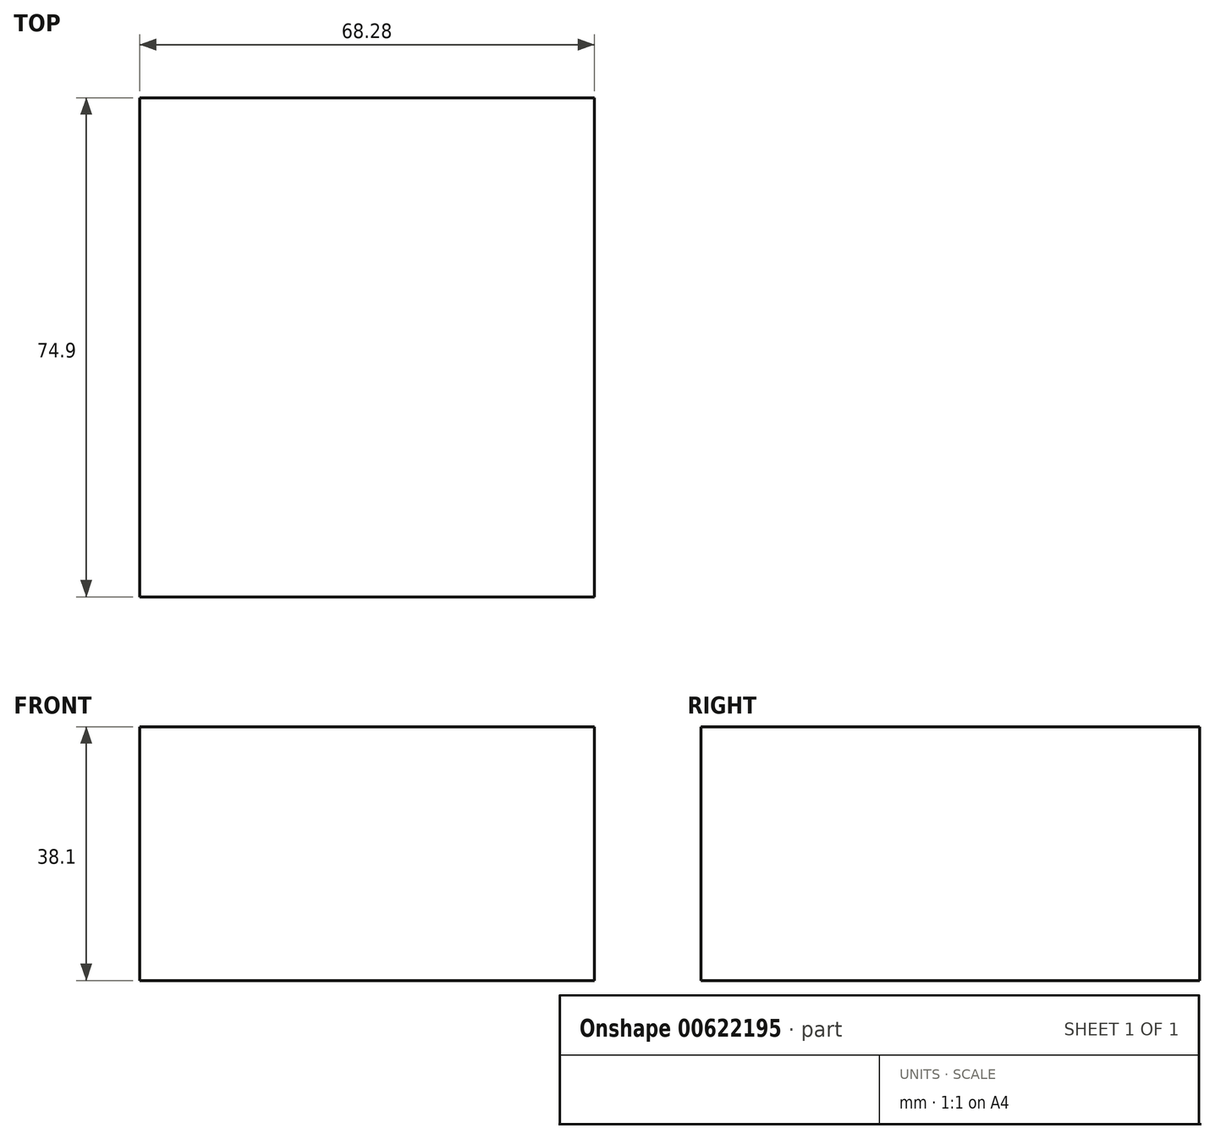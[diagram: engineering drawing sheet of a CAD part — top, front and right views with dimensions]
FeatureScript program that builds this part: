
annotation { "Feature Type Name" : "Feature", "Feature Type Description" : "" }
export const myFeature = defineFeature(function(context is Context, id is Id, definition is map)
    precondition{}
    {
        {
            var Q0;
            Q0=qCreatedBy(makeId("Top.planeOp"),FACE);
            var sketch = newSketch(context, id + "F0", { "sketchPlane" : qUnion([Q0])});
            skLineSegment(sketch, "E0.bottom", {"start": v(34.14, 37.45) * mm, "end": v(-34.14, 37.45) * mm});
            skLineSegment(sketch, "E0.top", {"start": v(34.14, -37.45) * mm, "end": v(-34.14, -37.45) * mm});
            skLineSegment(sketch, "E0.left", {"start": v(34.14, 37.45) * mm, "end": v(34.14, -37.45) * mm});
            skLineSegment(sketch, "E0.right", {"start": v(-34.14, 37.45) * mm, "end": v(-34.14, -37.45) * mm});
            skPoint(sketch, "E0.middle", {"position": v(0, 0) * mm});
            skSolve(sketch);
        }
        {
            var Q0;
            Q0=makeQuery(id+"F0.imprint","IMPRINT",FACE,{"disambiguationData":[TD([[makeQuery(id+"F0.imprint","IMPRINT",EDGE,{"derivedFrom":sQuery(id+"F0.wireOp",EDGE,"E0.bottom")}),1.0]])]});
            extrude(context, id + "F1", {"entities" : qUnion([Q0]), "depth" : 38.1 * mm, "offsetDistance" : 25.4 * mm});
        }
    });
